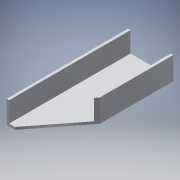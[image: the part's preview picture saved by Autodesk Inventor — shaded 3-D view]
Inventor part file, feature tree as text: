
AUTODESK INVENTOR PART (.ipt)
format: ipt  version: 2016 (Build 200138000, 138)  size: 110,592 bytes
history: native  units: in
note: dims shown in document units (in); Inventor stores cm internally (conversion verified against a paired STEP export)
features: extrude x2, sketch x2
ambient origin geometry x8: Origin, YZ Plane, XZ Plane, XY Plane, X Axis, Y Axis, Z Axis, Center Point
bodies: Solid1 (feature_tree)
feature tree (4):
  extrude  "Extrusion1"  Depth=1.125in
  extrude  "Extrusion4"  Depth=6.0in TaperAngle=0.0deg
  sketch  "Sketch1"  dims[d0=2.25in d1=1.125in]
  sketch  "Sketch5"  dims[d2=0.125in d3=6.0in d4=0.0in d14=3.65in d15=0.2611in d16=1.0in d17=0.0in d18=1.125in]
